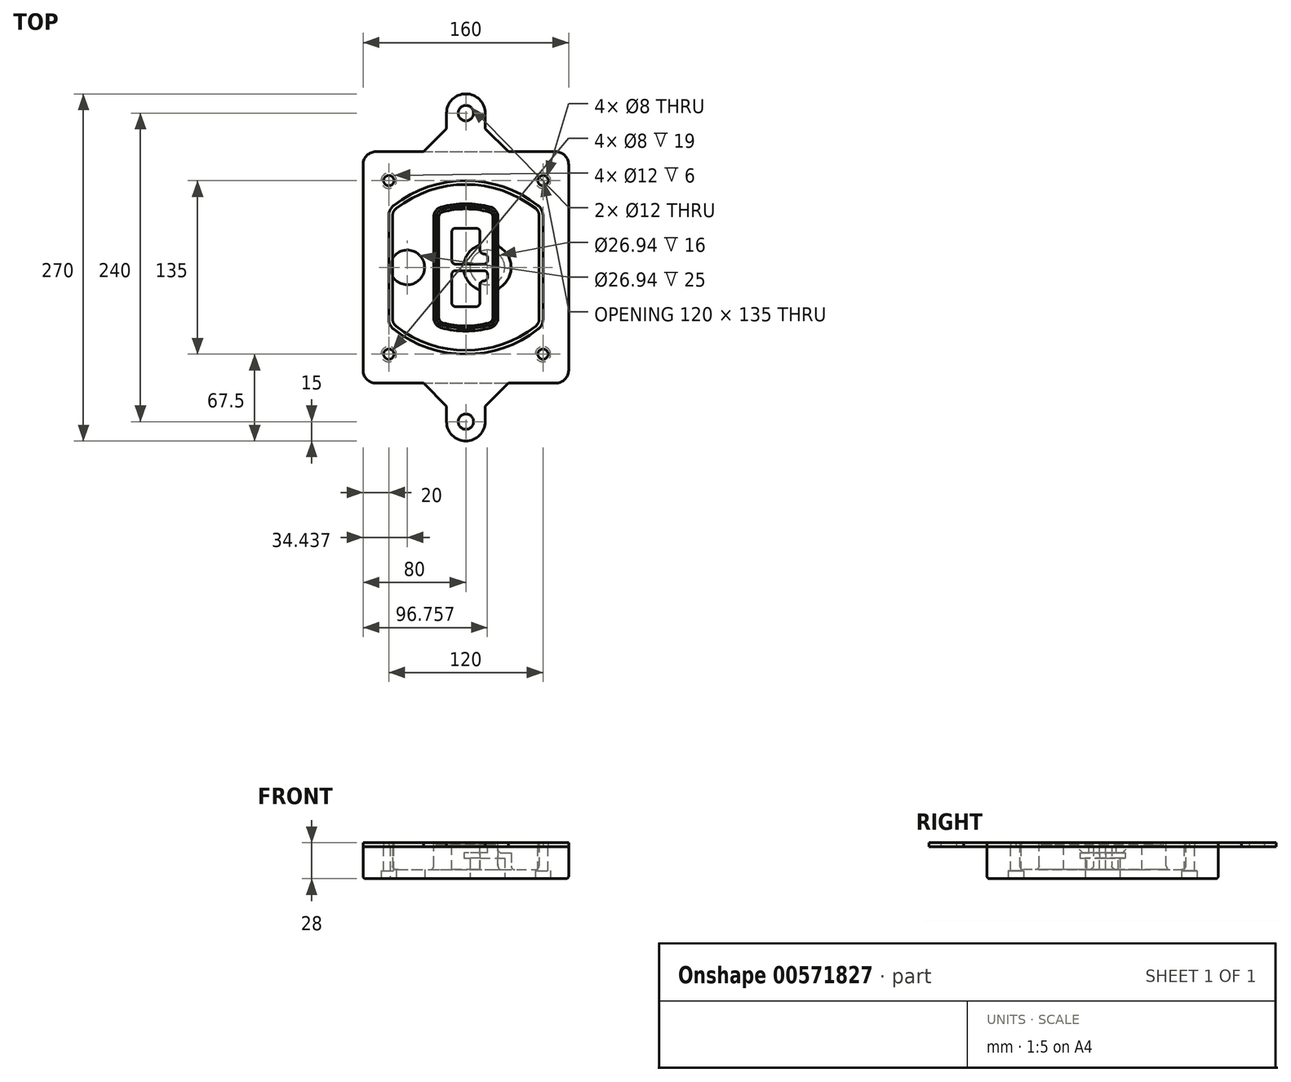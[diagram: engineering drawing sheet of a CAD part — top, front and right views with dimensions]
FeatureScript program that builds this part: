
annotation { "Feature Type Name" : "Feature", "Feature Type Description" : "" }
export const myFeature = defineFeature(function(context is Context, id is Id, definition is map)
    precondition{}
    {
        {
            var Q0;
            Q0=qCreatedBy(makeId("Top.planeOp"),FACE);
            var sketch = newSketch(context, id + "F0", { "sketchPlane" : qUnion([Q0])});
            skPoint(sketch, "E0.rect.middle", {"position": v(0, 0) * mm});
            skLineSegment(sketch, "E1.bottom", {"start": v(-70, -90) * mm, "end": v(70, -90) * mm});
            skLineSegment(sketch, "E1.top", {"start": v(-70, 90) * mm, "end": v(70, 90) * mm});
            skLineSegment(sketch, "E1.left", {"start": v(-80, -80) * mm, "end": v(-80, 80) * mm});
            skLineSegment(sketch, "E1.right", {"start": v(80, -80) * mm, "end": v(80, 80) * mm});
            skLineSegment(sketch, "E2", {"start": v(-80, 90) * mm, "end": v(80, -90) * mm, "construction": true});
            skLineSegment(sketch, "E3", {"start": v(80, 90) * mm, "end": v(-80, -90) * mm, "construction": true});
            skCircle(sketch, "E4", {"center": v(-60, 67.5) * mm, "radius": 4 * mm});
            skCircle(sketch, "E5", {"center": v(60, 67.5) * mm, "radius": 4 * mm});
            skCircle(sketch, "E6", {"center": v(60, -67.5) * mm, "radius": 4 * mm});
            skCircle(sketch, "E7", {"center": v(-60, -67.5) * mm, "radius": 4 * mm});
            skLineSegment(sketch, "E8", {"start": v(-60, 67.5) * mm, "end": v(60, 67.5) * mm, "construction": true});
            skLineSegment(sketch, "E9", {"start": v(60, 67.5) * mm, "end": v(60, -67.5) * mm, "construction": true});
            skLineSegment(sketch, "E10", {"start": v(60, -67.5) * mm, "end": v(-60, -67.5) * mm, "construction": true});
            skLineSegment(sketch, "E11", {"start": v(-60, -67.5) * mm, "end": v(-60, 67.5) * mm, "construction": true});
            skLineSegment(sketch, "E12", {"start": v(-60, 40.3) * mm, "end": v(-60, -40.3) * mm});
            skLineSegment(sketch, "E13", {"start": v(60, 40.3) * mm, "end": v(60, -40.3) * mm});
            skArc(sketch, "E14", {"start": v(56.15, 48.18) * mm, "mid": v(0, 67.5) * mm, "end": v(-56.15, 48.18) * mm});
            skArc(sketch, "E15", {"start": v(-56.15, -48.18) * mm, "mid": v(0, -67.5) * mm, "end": v(56.15, -48.18) * mm});
            skLineSegment(sketch, "E16", {"start": v(-60, 0) * mm, "end": v(60, 0) * mm, "construction": true});
            skPoint(sketch, "E17.visualSharp", {"position": v(-60, -45) * mm});
            skArc(sketch, "E17.filletArc", {"start": v(-60, -40.3) * mm, "mid": v(-58.99, -44.68) * mm, "end": v(-56.15, -48.18) * mm});
            skPoint(sketch, "E18.visualSharp", {"position": v(-60, 45) * mm});
            skArc(sketch, "E18.filletArc", {"start": v(-56.15, 48.18) * mm, "mid": v(-58.99, 44.68) * mm, "end": v(-60, 40.3) * mm});
            skPoint(sketch, "E19.visualSharp", {"position": v(60, 45) * mm});
            skArc(sketch, "E19.filletArc", {"start": v(60, 40.3) * mm, "mid": v(58.99, 44.68) * mm, "end": v(56.15, 48.18) * mm});
            skPoint(sketch, "E20.visualSharp", {"position": v(60, -45) * mm});
            skArc(sketch, "E20.filletArc", {"start": v(56.15, -48.18) * mm, "mid": v(58.99, -44.68) * mm, "end": v(60, -40.3) * mm});
            skPoint(sketch, "E21.visualSharp", {"position": v(-80, 90) * mm});
            skArc(sketch, "E21.filletArc", {"start": v(-70, 90) * mm, "mid": v(-77.07, 87.07) * mm, "end": v(-80, 80) * mm});
            skPoint(sketch, "E22.visualSharp", {"position": v(80, 90) * mm});
            skArc(sketch, "E22.filletArc", {"start": v(80, 80) * mm, "mid": v(77.07, 87.07) * mm, "end": v(70, 90) * mm});
            skPoint(sketch, "E23.visualSharp", {"position": v(80, -90) * mm});
            skArc(sketch, "E23.filletArc", {"start": v(70, -90) * mm, "mid": v(77.07, -87.07) * mm, "end": v(80, -80) * mm});
            skPoint(sketch, "E24.visualSharp", {"position": v(-80, -90) * mm});
            skArc(sketch, "E24.filletArc", {"start": v(-80, -80) * mm, "mid": v(-77.07, -87.07) * mm, "end": v(-70, -90) * mm});
            skArc(sketch, "E25.0", {"start": v(57, 40.3) * mm, "mid": v(56.3, 43.36) * mm, "end": v(54.3, 45.81) * mm});
            skLineSegment(sketch, "E25.1", {"start": v(57, 40.3) * mm, "end": v(57, -40.3) * mm});
            skArc(sketch, "E25.2", {"start": v(54.3, -45.81) * mm, "mid": v(56.3, -43.36) * mm, "end": v(57, -40.3) * mm});
            skArc(sketch, "E25.3", {"start": v(-54.3, -45.81) * mm, "mid": v(0, -64.5) * mm, "end": v(54.3, -45.81) * mm});
            skArc(sketch, "E25.4", {"start": v(-57, -40.3) * mm, "mid": v(-56.3, -43.36) * mm, "end": v(-54.3, -45.81) * mm});
            skArc(sketch, "E25.5", {"start": v(54.3, 45.81) * mm, "mid": v(0, 64.5) * mm, "end": v(-54.3, 45.81) * mm});
            skLineSegment(sketch, "E25.6", {"start": v(-57, 40.3) * mm, "end": v(-57, -40.3) * mm});
            skArc(sketch, "E25.7", {"start": v(-54.3, 45.81) * mm, "mid": v(-56.3, 43.36) * mm, "end": v(-57, 40.3) * mm});
            skArc(sketch, "E26.0", {"start": v(-58.62, 51.33) * mm, "mid": v(-62.58, 46.43) * mm, "end": v(-64, 40.3) * mm});
            skArc(sketch, "E26.1", {"start": v(58.62, 51.33) * mm, "mid": v(0, 71.5) * mm, "end": v(-58.62, 51.33) * mm});
            skArc(sketch, "E26.2", {"start": v(64, 40.3) * mm, "mid": v(62.58, 46.43) * mm, "end": v(58.62, 51.33) * mm});
            skLineSegment(sketch, "E26.3", {"start": v(64, 40.3) * mm, "end": v(64, -40.3) * mm});
            skArc(sketch, "E26.4", {"start": v(58.62, -51.33) * mm, "mid": v(62.58, -46.43) * mm, "end": v(64, -40.3) * mm});
            skLineSegment(sketch, "E26.5", {"start": v(-64, 40.3) * mm, "end": v(-64, -40.3) * mm});
            skArc(sketch, "E26.6", {"start": v(-58.62, -51.33) * mm, "mid": v(0, -71.5) * mm, "end": v(58.62, -51.33) * mm});
            skArc(sketch, "E26.7", {"start": v(-64, -40.3) * mm, "mid": v(-62.58, -46.43) * mm, "end": v(-58.62, -51.33) * mm});
            skSolve(sketch);
        }
        {
            var Q0;
            Q0=makeQuery(id+"F0.imprint","IMPRINT",FACE,{"disambiguationData":[TD([[makeQuery(id+"F0.imprint","IMPRINT",EDGE,{"derivedFrom":sQuery(id+"F0.wireOp",EDGE,"E1.bottom")}),1.0]])]});
            var Q1;
            Q1=makeQuery(id+"F0.imprint","IMPRINT",FACE,{"disambiguationData":[TD([[makeQuery(id+"F0.imprint","IMPRINT",EDGE,{"derivedFrom":sQuery(id+"F0.wireOp",EDGE,"E12")}),1.0]])]});
            var Q2;
            Q2=makeQuery(id+"F0.imprint","IMPRINT",FACE,{"disambiguationData":[TD([[makeQuery(id+"F0.imprint","IMPRINT",EDGE,{"derivedFrom":sQuery(id+"F0.wireOp",EDGE,"E25.0")}),1.0]])]});
            var Q3;
            Q3=makeQuery(id+"F0.imprint","IMPRINT",FACE,{"disambiguationData":[TD([[makeQuery(id+"F0.imprint","IMPRINT",EDGE,{"derivedFrom":sQuery(id+"F0.wireOp",EDGE,"E12")}),-1.0]])]});
            extrude(context, id + "F1", {"entities" : qUnion([Q0, Q1, Q2, Q3]), "oppositeDirection" : true, "depth" : 25 * mm});
        }
        {
            var Q0;
            Q0=makeQuery(id+"F0.imprint","IMPRINT",FACE,{"disambiguationData":[TD([[makeQuery(id+"F0.imprint","IMPRINT",EDGE,{"derivedFrom":sQuery(id+"F0.wireOp",EDGE,"E12")}),1.0]])]});
            extrude(context, id + "F2", {"entities" : qUnion([Q0]), "operationType" : NewBodyOperationType.ADD, "depth" : 3 * mm});
        }
        {
            var Q0;
            Q0=makeQuery(id+"F0.imprint","IMPRINT",FACE,{"disambiguationData":[TD([[makeQuery(id+"F0.imprint","IMPRINT",EDGE,{"derivedFrom":sQuery(id+"F0.wireOp",EDGE,"E25.0")}),1.0]])]});
            extrude(context, id + "F3", {"entities" : qUnion([Q0]), "operationType" : NewBodyOperationType.REMOVE, "oppositeDirection" : true, "depth" : 18 * mm});
        }
        {
            var Q0;
            Q0=makeQuery(id+"F2.opExtrude","CAP_FACE",FACE,{"disambiguationData":[OSD([sQuery(id+"F0.wireOp",EDGE,"E12"),sQuery(id+"F0.wireOp",EDGE,"E13"),sQuery(id+"F0.wireOp",EDGE,"E14"),sQuery(id+"F0.wireOp",EDGE,"E15"),sQuery(id+"F0.wireOp",EDGE,"E17.filletArc"),sQuery(id+"F0.wireOp",EDGE,"E18.filletArc"),sQuery(id+"F0.wireOp",EDGE,"E19.filletArc"),sQuery(id+"F0.wireOp",EDGE,"E20.filletArc"),sQuery(id+"F0.wireOp",EDGE,"E25.0"),sQuery(id+"F0.wireOp",EDGE,"E25.1"),sQuery(id+"F0.wireOp",EDGE,"E25.2"),sQuery(id+"F0.wireOp",EDGE,"E25.3"),sQuery(id+"F0.wireOp",EDGE,"E25.4"),sQuery(id+"F0.wireOp",EDGE,"E25.5"),sQuery(id+"F0.wireOp",EDGE,"E25.6"),sQuery(id+"F0.wireOp",EDGE,"E25.7")])],"isStart":false});
            var sketch = newSketch(context, id + "F4", { "sketchPlane" : qUnion([Q0])});
            skArc(sketch, "E27.0", {"start": v(-19.08, -46.97) * mm, "mid": v(0, -49.5) * mm, "end": v(19.08, -46.97) * mm});
            skArc(sketch, "E28.0", {"start": v(19.08, 46.97) * mm, "mid": v(0, 49.5) * mm, "end": v(-19.08, 46.97) * mm});
            skLineSegment(sketch, "E29", {"start": v(-25, 39.25) * mm, "end": v(-25, -39.25) * mm});
            skLineSegment(sketch, "E30", {"start": v(25, 39.25) * mm, "end": v(25, -39.25) * mm});
            skLineSegment(sketch, "E31", {"start": v(-25, 45.1) * mm, "end": v(25, 45.1) * mm, "construction": true});
            skLineSegment(sketch, "E32", {"start": v(-25, -45.1) * mm, "end": v(25, -45.1) * mm, "construction": true});
            skPoint(sketch, "E33.visualSharp", {"position": v(-25, 45.1) * mm});
            skArc(sketch, "E33.filletArc", {"start": v(-19.08, 46.97) * mm, "mid": v(-23.35, 44.11) * mm, "end": v(-25, 39.25) * mm});
            skPoint(sketch, "E34.visualSharp", {"position": v(25, 45.1) * mm});
            skArc(sketch, "E34.filletArc", {"start": v(25, 39.25) * mm, "mid": v(23.35, 44.11) * mm, "end": v(19.08, 46.97) * mm});
            skPoint(sketch, "E35.visualSharp", {"position": v(25, -45.1) * mm});
            skArc(sketch, "E35.filletArc", {"start": v(19.08, -46.97) * mm, "mid": v(23.35, -44.11) * mm, "end": v(25, -39.25) * mm});
            skPoint(sketch, "E36.visualSharp", {"position": v(-25, -45.1) * mm});
            skArc(sketch, "E36.filletArc", {"start": v(-25, -39.25) * mm, "mid": v(-23.35, -44.11) * mm, "end": v(-19.08, -46.97) * mm});
            skArc(sketch, "E37.0", {"start": v(54.3, 45.81) * mm, "mid": v(0, 64.5) * mm, "end": v(-54.3, 45.81) * mm});
            skArc(sketch, "E37.1", {"start": v(-54.3, 45.81) * mm, "mid": v(-56.3, 43.36) * mm, "end": v(-57, 40.3) * mm});
            skLineSegment(sketch, "E37.2", {"start": v(-57, 40.3) * mm, "end": v(-57, -40.3) * mm});
            skArc(sketch, "E37.3", {"start": v(-57, -40.3) * mm, "mid": v(-56.3, -43.36) * mm, "end": v(-54.3, -45.81) * mm});
            skArc(sketch, "E37.4", {"start": v(-54.3, -45.81) * mm, "mid": v(0, -64.5) * mm, "end": v(54.3, -45.81) * mm});
            skArc(sketch, "E37.5", {"start": v(54.3, -45.81) * mm, "mid": v(56.3, -43.36) * mm, "end": v(57, -40.3) * mm});
            skLineSegment(sketch, "E37.6", {"start": v(57, 40.3) * mm, "end": v(57, -40.3) * mm});
            skArc(sketch, "E37.7", {"start": v(57, 40.3) * mm, "mid": v(56.3, 43.36) * mm, "end": v(54.3, 45.81) * mm});
            skLineSegment(sketch, "E38.0", {"start": v(23, 39.25) * mm, "end": v(23, -39.25) * mm});
            skArc(sketch, "E38.1", {"start": v(18.56, -45.04) * mm, "mid": v(21.76, -42.9) * mm, "end": v(23, -39.25) * mm});
            skArc(sketch, "E38.2", {"start": v(-18.56, -45.04) * mm, "mid": v(0, -47.5) * mm, "end": v(18.56, -45.04) * mm});
            skArc(sketch, "E38.3", {"start": v(-23, -39.25) * mm, "mid": v(-21.76, -42.9) * mm, "end": v(-18.56, -45.04) * mm});
            skLineSegment(sketch, "E38.4", {"start": v(-23, 39.25) * mm, "end": v(-23, -39.25) * mm});
            skArc(sketch, "E38.5", {"start": v(23, 39.25) * mm, "mid": v(21.76, 42.9) * mm, "end": v(18.56, 45.04) * mm});
            skArc(sketch, "E38.6", {"start": v(-18.56, 45.04) * mm, "mid": v(-21.76, 42.9) * mm, "end": v(-23, 39.25) * mm});
            skArc(sketch, "E38.7", {"start": v(18.56, 45.04) * mm, "mid": v(0, 47.5) * mm, "end": v(-18.56, 45.04) * mm});
            skArc(sketch, "E39.0", {"start": v(21, 39.25) * mm, "mid": v(20.18, 41.68) * mm, "end": v(18.04, 43.1) * mm});
            skLineSegment(sketch, "E39.1", {"start": v(21, 39.25) * mm, "end": v(21, -39.25) * mm});
            skArc(sketch, "E39.2", {"start": v(18.04, -43.1) * mm, "mid": v(20.18, -41.68) * mm, "end": v(21, -39.25) * mm});
            skArc(sketch, "E39.3", {"start": v(-18.04, -43.1) * mm, "mid": v(0, -45.5) * mm, "end": v(18.04, -43.1) * mm});
            skArc(sketch, "E39.4", {"start": v(-21, -39.25) * mm, "mid": v(-20.18, -41.68) * mm, "end": v(-18.04, -43.1) * mm});
            skArc(sketch, "E39.5", {"start": v(18.04, 43.1) * mm, "mid": v(0, 45.5) * mm, "end": v(-18.04, 43.1) * mm});
            skLineSegment(sketch, "E39.6", {"start": v(-21, 39.25) * mm, "end": v(-21, -39.25) * mm});
            skArc(sketch, "E39.7", {"start": v(-18.04, 43.1) * mm, "mid": v(-20.18, 41.68) * mm, "end": v(-21, 39.25) * mm});
            skLineSegment(sketch, "E40", {"start": v(-25, 0) * mm, "end": v(25, 0) * mm, "construction": true});
            skLineSegment(sketch, "E41", {"start": v(-11, 5.5) * mm, "end": v(-11, 27.5) * mm});
            skLineSegment(sketch, "E42", {"start": v(-8, 30.5) * mm, "end": v(8, 30.5) * mm});
            skLineSegment(sketch, "E43", {"start": v(11, 27.5) * mm, "end": v(11, 13.5) * mm});
            skLineSegment(sketch, "E44", {"start": v(14, 10.5) * mm, "end": v(14, 10.5) * mm});
            skLineSegment(sketch, "E45", {"start": v(17, 7.5) * mm, "end": v(17, 5.5) * mm});
            skLineSegment(sketch, "E46", {"start": v(14, 2.5) * mm, "end": v(-8, 2.5) * mm});
            skPoint(sketch, "E47.visualSharp", {"position": v(-11, 30.5) * mm});
            skArc(sketch, "E47.filletArc", {"start": v(-8, 30.5) * mm, "mid": v(-10.12, 29.62) * mm, "end": v(-11, 27.5) * mm});
            skPoint(sketch, "E48.visualSharp", {"position": v(11, 30.5) * mm});
            skArc(sketch, "E48.filletArc", {"start": v(11, 27.5) * mm, "mid": v(10.12, 29.62) * mm, "end": v(8, 30.5) * mm});
            skPoint(sketch, "E49.visualSharp", {"position": v(11, 10.5) * mm});
            skArc(sketch, "E49.filletArc", {"start": v(11, 13.5) * mm, "mid": v(11.88, 11.38) * mm, "end": v(14, 10.5) * mm});
            skPoint(sketch, "E50.visualSharp", {"position": v(17, 10.5) * mm});
            skArc(sketch, "E50.filletArc", {"start": v(17, 7.5) * mm, "mid": v(16.12, 9.62) * mm, "end": v(14, 10.5) * mm});
            skPoint(sketch, "E51.visualSharp", {"position": v(17, 2.5) * mm});
            skArc(sketch, "E51.filletArc", {"start": v(14, 2.5) * mm, "mid": v(16.12, 3.38) * mm, "end": v(17, 5.5) * mm});
            skPoint(sketch, "E52.visualSharp", {"position": v(-11, 2.5) * mm});
            skArc(sketch, "E52.filletArc", {"start": v(-11, 5.5) * mm, "mid": v(-10.12, 3.38) * mm, "end": v(-8, 2.5) * mm});
            skLineSegment(sketch, "E53.0.MirrorCS", {"start": v(14, -2.5) * mm, "end": v(-8, -2.5) * mm});
            skArc(sketch, "E54.0.MirrorCS", {"start": v(-11, -5.5) * mm, "mid": v(-10.12, -3.38) * mm, "end": v(-8, -2.5) * mm});
            skLineSegment(sketch, "E55.0.MirrorCS", {"start": v(-11, -5.5) * mm, "end": v(-11, -27.5) * mm});
            skArc(sketch, "E56.0.MirrorCS", {"start": v(-8, -30.5) * mm, "mid": v(-10.12, -29.62) * mm, "end": v(-11, -27.5) * mm});
            skLineSegment(sketch, "E57.0.MirrorCS", {"start": v(-8, -30.5) * mm, "end": v(8, -30.5) * mm});
            skArc(sketch, "E58.0.MirrorCS", {"start": v(11, -27.5) * mm, "mid": v(10.12, -29.62) * mm, "end": v(8, -30.5) * mm});
            skLineSegment(sketch, "E59.0.MirrorCS", {"start": v(11, -27.5) * mm, "end": v(11, -13.5) * mm});
            skArc(sketch, "E60.0.MirrorCS", {"start": v(11, -13.5) * mm, "mid": v(11.88, -11.38) * mm, "end": v(14, -10.5) * mm});
            skArc(sketch, "E61.0.MirrorCS", {"start": v(17, -7.5) * mm, "mid": v(16.12, -9.62) * mm, "end": v(14, -10.5) * mm});
            skLineSegment(sketch, "E62.0.MirrorCS", {"start": v(17, -7.5) * mm, "end": v(17, -5.5) * mm});
            skArc(sketch, "E63.0.MirrorCS", {"start": v(14, -2.5) * mm, "mid": v(16.12, -3.38) * mm, "end": v(17, -5.5) * mm});
            skSolve(sketch);
        }
        {
            var Q0;
            Q0=makeQuery(id+"F4.imprint","IMPRINT",FACE,{"disambiguationData":[TD([[makeQuery(id+"F4.imprint","IMPRINT",EDGE,{"derivedFrom":sQuery(id+"F4.wireOp",EDGE,"E27.0")}),1.0]])]});
            var Q1;
            Q1=makeQuery(id+"F4.imprint","IMPRINT",FACE,{"disambiguationData":[TD([[makeQuery(id+"F4.imprint","IMPRINT",EDGE,{"derivedFrom":sQuery(id+"F4.wireOp",EDGE,"E38.0")}),-1.0]])]});
            var Q2;
            Q2=makeQuery(id+"F4.imprint","IMPRINT",FACE,{"disambiguationData":[TD([[makeQuery(id+"F4.imprint","IMPRINT",EDGE,{"derivedFrom":sQuery(id+"F4.wireOp",EDGE,"E39.0")}),1.0]])]});
            extrude(context, id + "F5", {"entities" : qUnion([Q0, Q1, Q2]), "operationType" : NewBodyOperationType.ADD, "endBound" : BoundingType.UP_TO_NEXT, "oppositeDirection" : true, "depth" : 25 * mm});
        }
        {
            var Q0;
            Q0=makeQuery(id+"F4.imprint","IMPRINT",FACE,{"disambiguationData":[TD([[makeQuery(id+"F4.imprint","IMPRINT",EDGE,{"derivedFrom":sQuery(id+"F4.wireOp",EDGE,"E38.0")}),-1.0]])]});
            extrude(context, id + "F6", {"entities" : qUnion([Q0]), "operationType" : NewBodyOperationType.REMOVE, "oppositeDirection" : true, "depth" : 2 * mm});
        }
        {
            var Q0;
            Q0=makeQuery(id+"F1.opExtrude","CAP_FACE",FACE,{"disambiguationData":[OSD([sQuery(id+"F0.wireOp",EDGE,"E1.bottom"),sQuery(id+"F0.wireOp",EDGE,"E1.top"),sQuery(id+"F0.wireOp",EDGE,"E1.left"),sQuery(id+"F0.wireOp",EDGE,"E1.right"),sQuery(id+"F0.wireOp",EDGE,"E4"),sQuery(id+"F0.wireOp",EDGE,"E5"),sQuery(id+"F0.wireOp",EDGE,"E6"),sQuery(id+"F0.wireOp",EDGE,"E7"),sQuery(id+"F0.wireOp",EDGE,"E21.filletArc"),sQuery(id+"F0.wireOp",EDGE,"E22.filletArc"),sQuery(id+"F0.wireOp",EDGE,"E23.filletArc"),sQuery(id+"F0.wireOp",EDGE,"E24.filletArc")])],"isStart":false});
            var sketch = newSketch(context, id + "F7", { "sketchPlane" : qUnion([Q0])});
            skCircle(sketch, "E64", {"center": v(16.76, 0) * mm, "radius": 13.47 * mm});
            skCircle(sketch, "E65", {"center": v(-45.56, 0) * mm, "radius": 13.47 * mm});
            skLineSegment(sketch, "E66", {"start": v(80, 0) * mm, "end": v(-80, 0) * mm});
            skCircle(sketch, "E67", {"center": v(16.76, 0) * mm, "radius": 18.47 * mm});
            skCircle(sketch, "E68", {"center": v(60, -67.5) * mm, "radius": 6 * mm});
            skCircle(sketch, "E69", {"center": v(-60, -67.5) * mm, "radius": 6 * mm});
            skCircle(sketch, "E70", {"center": v(-60, 67.5) * mm, "radius": 6 * mm});
            skCircle(sketch, "E71", {"center": v(60, 67.5) * mm, "radius": 6 * mm});
            skSolve(sketch);
        }
        {
            var Q0;
            {var subQ1=sQuery(id+"F7.wireOp",EDGE,"E66");var subQ4=sQuery(id+"F7.wireOp",EDGE,"E64");var subQ6=makeQuery(id+"F7.imprint","INTERSECT",VERTEX,{"disambiguationData":[OD(0.0)],"derivedFrom":[subQ4,subQ1]});Q0=makeQuery(id+"F7.imprint","IMPRINT",FACE,{"disambiguationData":[TD([[makeQuery(id+"F7.imprint","IMPRINT",EDGE,{"disambiguationData":[TD([[subQ6,-1.0]])],"derivedFrom":subQ4}),-1.0]])]});}
            var Q1;
            {var subQ0=sQuery(id+"F7.wireOp",EDGE,"E66");var subQ1=sQuery(id+"F7.wireOp",EDGE,"E64");var subQ3=makeQuery(id+"F7.imprint","INTERSECT",VERTEX,{"disambiguationData":[OD(0.0)],"derivedFrom":[subQ1,subQ0]});Q1=makeQuery(id+"F7.imprint","IMPRINT",FACE,{"disambiguationData":[TD([[makeQuery(id+"F7.imprint","IMPRINT",EDGE,{"disambiguationData":[TD([[subQ3,-1.0]])],"derivedFrom":subQ1}),1.0]])]});}
            var Q2;
            {var subQ0=sQuery(id+"F7.wireOp",EDGE,"E66");var subQ1=sQuery(id+"F7.wireOp",EDGE,"E64");var subQ3=makeQuery(id+"F7.imprint","INTERSECT",VERTEX,{"disambiguationData":[OD(0.0)],"derivedFrom":[subQ1,subQ0]});Q2=makeQuery(id+"F7.imprint","IMPRINT",FACE,{"disambiguationData":[TD([[makeQuery(id+"F7.imprint","IMPRINT",EDGE,{"disambiguationData":[TD([[subQ3,1.0]])],"derivedFrom":subQ1}),1.0]])]});}
            var Q3;
            {var subQ1=sQuery(id+"F7.wireOp",EDGE,"E66");var subQ4=sQuery(id+"F7.wireOp",EDGE,"E64");var subQ6=makeQuery(id+"F7.imprint","INTERSECT",VERTEX,{"disambiguationData":[OD(0.0)],"derivedFrom":[subQ4,subQ1]});Q3=makeQuery(id+"F7.imprint","IMPRINT",FACE,{"disambiguationData":[TD([[makeQuery(id+"F7.imprint","IMPRINT",EDGE,{"disambiguationData":[TD([[subQ6,1.0]])],"derivedFrom":subQ4}),-1.0]])]});}
            extrude(context, id + "F8", {"entities" : qUnion([Q0, Q1, Q2, Q3]), "operationType" : NewBodyOperationType.ADD, "oppositeDirection" : true, "depth" : 20 * mm});
        }
        {
            var Q0;
            {var subQ0=sQuery(id+"F7.wireOp",EDGE,"E66");var subQ1=sQuery(id+"F7.wireOp",EDGE,"E64");var subQ3=makeQuery(id+"F7.imprint","INTERSECT",VERTEX,{"disambiguationData":[OD(0.0)],"derivedFrom":[subQ1,subQ0]});Q0=makeQuery(id+"F7.imprint","IMPRINT",FACE,{"disambiguationData":[TD([[makeQuery(id+"F7.imprint","IMPRINT",EDGE,{"disambiguationData":[TD([[subQ3,-1.0]])],"derivedFrom":subQ1}),1.0]])]});}
            var Q1;
            {var subQ0=sQuery(id+"F7.wireOp",EDGE,"E66");var subQ1=sQuery(id+"F7.wireOp",EDGE,"E64");var subQ3=makeQuery(id+"F7.imprint","INTERSECT",VERTEX,{"disambiguationData":[OD(0.0)],"derivedFrom":[subQ1,subQ0]});Q1=makeQuery(id+"F7.imprint","IMPRINT",FACE,{"disambiguationData":[TD([[makeQuery(id+"F7.imprint","IMPRINT",EDGE,{"disambiguationData":[TD([[subQ3,1.0]])],"derivedFrom":subQ1}),1.0]])]});}
            extrude(context, id + "F9", {"entities" : qUnion([Q0, Q1]), "operationType" : NewBodyOperationType.REMOVE, "oppositeDirection" : true, "depth" : 16 * mm});
        }
        {
            var Q0;
            {var subQ0=sQuery(id+"F7.wireOp",EDGE,"E66");var subQ1=sQuery(id+"F7.wireOp",EDGE,"E65");var subQ3=makeQuery(id+"F7.imprint","INTERSECT",VERTEX,{"disambiguationData":[OD(0.0)],"derivedFrom":[subQ1,subQ0]});Q0=makeQuery(id+"F7.imprint","IMPRINT",FACE,{"disambiguationData":[TD([[makeQuery(id+"F7.imprint","IMPRINT",EDGE,{"disambiguationData":[TD([[subQ3,-1.0]])],"derivedFrom":subQ1}),1.0]])]});}
            var Q1;
            {var subQ0=sQuery(id+"F7.wireOp",EDGE,"E66");var subQ1=sQuery(id+"F7.wireOp",EDGE,"E65");var subQ3=makeQuery(id+"F7.imprint","INTERSECT",VERTEX,{"disambiguationData":[OD(0.0)],"derivedFrom":[subQ1,subQ0]});Q1=makeQuery(id+"F7.imprint","IMPRINT",FACE,{"disambiguationData":[TD([[makeQuery(id+"F7.imprint","IMPRINT",EDGE,{"disambiguationData":[TD([[subQ3,1.0]])],"derivedFrom":subQ1}),1.0]])]});}
            extrude(context, id + "F10", {"entities" : qUnion([Q0, Q1]), "operationType" : NewBodyOperationType.REMOVE, "oppositeDirection" : true, "depth" : 25 * mm});
        }
        {
            var Q0;
            Q0=makeQuery(id+"F7.imprint","IMPRINT",FACE,{"disambiguationData":[TD([[makeQuery(id+"F7.imprint","IMPRINT",EDGE,{"derivedFrom":sQuery(id+"F7.wireOp",EDGE,"E68")}),1.0]])]});
            var Q1;
            Q1=makeQuery(id+"F7.imprint","IMPRINT",FACE,{"disambiguationData":[TD([[makeQuery(id+"F7.imprint","IMPRINT",EDGE,{"derivedFrom":makeQuery(id+"F1.opExtrude","CAP_EDGE",EDGE,{"disambiguationData":[OSD([sQuery(id+"F0.wireOp",EDGE,"E5")])],"isStart":false})}),-1.0]])]});
            var Q2;
            Q2=makeQuery(id+"F7.imprint","IMPRINT",FACE,{"disambiguationData":[TD([[makeQuery(id+"F7.imprint","IMPRINT",EDGE,{"derivedFrom":sQuery(id+"F7.wireOp",EDGE,"E69")}),1.0]])]});
            var Q3;
            Q3=makeQuery(id+"F7.imprint","IMPRINT",FACE,{"disambiguationData":[TD([[makeQuery(id+"F7.imprint","IMPRINT",EDGE,{"derivedFrom":makeQuery(id+"F1.opExtrude","CAP_EDGE",EDGE,{"disambiguationData":[OSD([sQuery(id+"F0.wireOp",EDGE,"E4")])],"isStart":false})}),-1.0]])]});
            var Q4;
            Q4=makeQuery(id+"F7.imprint","IMPRINT",FACE,{"disambiguationData":[TD([[makeQuery(id+"F7.imprint","IMPRINT",EDGE,{"derivedFrom":sQuery(id+"F7.wireOp",EDGE,"E70")}),1.0]])]});
            var Q5;
            Q5=makeQuery(id+"F7.imprint","IMPRINT",FACE,{"disambiguationData":[TD([[makeQuery(id+"F7.imprint","IMPRINT",EDGE,{"derivedFrom":makeQuery(id+"F1.opExtrude","CAP_EDGE",EDGE,{"disambiguationData":[OSD([sQuery(id+"F0.wireOp",EDGE,"E7")])],"isStart":false})}),-1.0]])]});
            var Q6;
            Q6=makeQuery(id+"F7.imprint","IMPRINT",FACE,{"disambiguationData":[TD([[makeQuery(id+"F7.imprint","IMPRINT",EDGE,{"derivedFrom":sQuery(id+"F7.wireOp",EDGE,"E71")}),1.0]])]});
            var Q7;
            Q7=makeQuery(id+"F7.imprint","IMPRINT",FACE,{"disambiguationData":[TD([[makeQuery(id+"F7.imprint","IMPRINT",EDGE,{"derivedFrom":makeQuery(id+"F1.opExtrude","CAP_EDGE",EDGE,{"disambiguationData":[OSD([sQuery(id+"F0.wireOp",EDGE,"E6")])],"isStart":false})}),-1.0]])]});
            extrude(context, id + "F11", {"entities" : qUnion([Q0, Q1, Q2, Q3, Q4, Q5, Q6, Q7]), "operationType" : NewBodyOperationType.REMOVE, "oppositeDirection" : true, "depth" : 6 * mm});
        }
        {
            var Q0;
            Q0=makeQuery(id+"F9.boolean.opBoolean","COPY",FACE,{"derivedFrom":makeQuery(id+"F9.opExtrude","CAP_FACE",FACE,{"disambiguationData":[OSD([sQuery(id+"F7.wireOp",EDGE,"E64")])],"isStart":false})});
            var sketch = newSketch(context, id + "F12", { "sketchPlane" : qUnion([Q0])});
            skArc(sketch, "E72.0", {"start": v(11, 17.55) * mm, "mid": v(2.57, 11.82) * mm, "end": v(-1.54, 2.5) * mm});
            skArc(sketch, "E72.1", {"start": v(-1.54, -2.5) * mm, "mid": v(2.57, -11.82) * mm, "end": v(11, -17.55) * mm});
            skLineSegment(sketch, "E73", {"start": v(-1.54, -2.5) * mm, "end": v(14, -2.5) * mm});
            skLineSegment(sketch, "E74.0", {"start": v(14, 2.5) * mm, "end": v(-1.54, 2.5) * mm});
            skArc(sketch, "E74.1", {"start": v(14, 2.5) * mm, "mid": v(16.12, 3.38) * mm, "end": v(17, 5.5) * mm});
            skLineSegment(sketch, "E74.2", {"start": v(17, 7.5) * mm, "end": v(17, 5.5) * mm});
            skArc(sketch, "E74.3", {"start": v(17, 7.5) * mm, "mid": v(16.12, 9.62) * mm, "end": v(14, 10.5) * mm});
            skArc(sketch, "E74.4", {"start": v(11, 13.5) * mm, "mid": v(11.88, 11.38) * mm, "end": v(14, 10.5) * mm});
            skLineSegment(sketch, "E74.5", {"start": v(11, 17.55) * mm, "end": v(11, 13.5) * mm});
            skLineSegment(sketch, "E74.7", {"start": v(14, -2.5) * mm, "end": v(-1.54, -2.5) * mm});
            skArc(sketch, "E74.8", {"start": v(14, -2.5) * mm, "mid": v(16.12, -3.38) * mm, "end": v(17, -5.5) * mm});
            skLineSegment(sketch, "E74.9", {"start": v(17, -7.5) * mm, "end": v(17, -5.5) * mm});
            skArc(sketch, "E74.10", {"start": v(17, -7.5) * mm, "mid": v(16.12, -9.62) * mm, "end": v(14, -10.5) * mm});
            skArc(sketch, "E74.11", {"start": v(11, -13.5) * mm, "mid": v(11.88, -11.38) * mm, "end": v(14, -10.5) * mm});
            skLineSegment(sketch, "E74.12", {"start": v(11, -17.55) * mm, "end": v(11, -13.5) * mm});
            skPoint(sketch, "E75.orphan", {"position": v(11, -27.5) * mm});
            skPoint(sketch, "E76.orphan", {"position": v(-8, -2.5) * mm});
            skPoint(sketch, "E77.orphan", {"position": v(-8, 2.5) * mm});
            skPoint(sketch, "E78.orphan", {"position": v(11, 27.5) * mm});
            skSolve(sketch);
        }
        {
            var Q0;
            {var subQ7=sQuery(id+"F12.wireOp",EDGE,"E72.0");var subQ14=sQuery(id+"F12.wireOp",EDGE,"E72.1");var subQ16=sQuery(id+"F12.wireOp",EDGE,"E74.1");var subQ18=sQuery(id+"F12.wireOp",EDGE,"E74.8");Q0=qUnion([makeQuery(id+"F12.imprint","IMPRINT",FACE,{"disambiguationData":[TD([[makeQuery(id+"F12.imprint","IMPRINT",EDGE,{"derivedFrom":subQ7}),1.0]])]}),makeQuery(id+"F12.imprint","IMPRINT",FACE,{"disambiguationData":[TD([[makeQuery(id+"F12.imprint","IMPRINT",EDGE,{"derivedFrom":subQ14}),1.0]])]}),makeQuery(id+"F12.imprint","IMPRINT",FACE,{"disambiguationData":[TD([[makeQuery(id+"F12.imprint","IMPRINT",EDGE,{"derivedFrom":subQ16}),1.0]])]}),makeQuery(id+"F12.imprint","IMPRINT",FACE,{"disambiguationData":[TD([[makeQuery(id+"F12.imprint","IMPRINT",EDGE,{"derivedFrom":subQ18}),-1.0]])]})]);}
            var Q1;
            Q1=makeQuery(id+"F5.boolean.opBoolean","SPLIT",FACE,{"disambiguationData":[TD([makeQuery(id+"F5.opExtrude","SWEPT_FACE",FACE,{"disambiguationData":[OSD([sQuery(id+"F4.wireOp",EDGE,"E41")])]})])],"derivedFrom":makeQuery(id+"F3.boolean.opBoolean","COPY",FACE,{"derivedFrom":makeQuery(id+"F3.opExtrude","CAP_FACE",FACE,{"disambiguationData":[OSD([sQuery(id+"F0.wireOp",EDGE,"E25.0"),sQuery(id+"F0.wireOp",EDGE,"E25.1"),sQuery(id+"F0.wireOp",EDGE,"E25.2"),sQuery(id+"F0.wireOp",EDGE,"E25.3"),sQuery(id+"F0.wireOp",EDGE,"E25.4"),sQuery(id+"F0.wireOp",EDGE,"E25.5"),sQuery(id+"F0.wireOp",EDGE,"E25.6"),sQuery(id+"F0.wireOp",EDGE,"E25.7")])],"isStart":false})})});
            extrude(context, id + "F13", {"entities" : qUnion([Q0]), "operationType" : NewBodyOperationType.REMOVE, "endBound" : BoundingType.UP_TO_SURFACE, "endBoundEntityFace" : qUnion([Q1]), "depth" : 25 * mm});
        }
        {
            var Q0;
            Q0=makeQuery(id+"F3.boolean.opBoolean","COPY",EDGE,{"derivedFrom":makeQuery(id+"F3.opExtrude","CAP_EDGE",EDGE,{"disambiguationData":[OSD([sQuery(id+"F0.wireOp",EDGE,"E25.6")])],"isStart":false})});
            var Q1;
            Q1=makeQuery(id+"F8.boolean.opBoolean","INTERSECT",EDGE,{"derivedFrom":[makeQuery(id+"F5.opExtrude","SWEPT_FACE",FACE,{"disambiguationData":[OSD([sQuery(id+"F4.wireOp",EDGE,"E30")])]}),makeQuery(id+"F8.opExtrude","CAP_FACE",FACE,{"disambiguationData":[OSD([sQuery(id+"F7.wireOp",EDGE,"E67")])],"isStart":false})]});
            var Q2;
            Q2=makeQuery(id+"F8.boolean.opBoolean","INTERSECT",EDGE,{"disambiguationData":[OD(1.0)],"derivedFrom":[makeQuery(id+"F5.opExtrude","SWEPT_FACE",FACE,{"disambiguationData":[OSD([sQuery(id+"F4.wireOp",EDGE,"E30")])]}),makeQuery(id+"F8.opExtrude","SWEPT_FACE",FACE,{"disambiguationData":[OSD([sQuery(id+"F7.wireOp",EDGE,"E67")])]})]});
            var Q3;
            {var subQ0=sQuery(id+"F4.wireOp",EDGE,"E30");Q3=makeQuery(id+"F8.boolean.opBoolean","SPLIT",EDGE,{"disambiguationData":[TD([makeQuery(id+"F5.opExtrude","SWEPT_FACE",FACE,{"disambiguationData":[OSD([sQuery(id+"F4.wireOp",EDGE,"E35.filletArc")])]})])],"derivedFrom":makeQuery(id+"F5.opExtrude","CAP_EDGE",EDGE,{"disambiguationData":[OSD([subQ0])],"isStart":false})});}
            var Q4;
            {var subQ0=sQuery(id+"F0.wireOp",EDGE,"E25.7");var subQ1=sQuery(id+"F0.wireOp",EDGE,"E25.1");var subQ2=sQuery(id+"F0.wireOp",EDGE,"E25.6");var subQ3=sQuery(id+"F0.wireOp",EDGE,"E25.5");var subQ4=sQuery(id+"F0.wireOp",EDGE,"E25.4");var subQ5=sQuery(id+"F0.wireOp",EDGE,"E25.0");var subQ6=sQuery(id+"F0.wireOp",EDGE,"E25.2");var subQ7=sQuery(id+"F0.wireOp",EDGE,"E25.3");Q4=makeQuery(id+"F8.boolean.opBoolean","INTERSECT",EDGE,{"derivedFrom":[makeQuery(id+"F5.boolean.opBoolean","SPLIT",FACE,{"disambiguationData":[TD([makeQuery(id+"F2.opExtrude","SWEPT_FACE",FACE,{"disambiguationData":[OSD([subQ5])]})])],"derivedFrom":makeQuery(id+"F3.boolean.opBoolean","COPY",FACE,{"derivedFrom":makeQuery(id+"F3.opExtrude","CAP_FACE",FACE,{"disambiguationData":[OSD([subQ5,subQ1,subQ6,subQ7,subQ4,subQ3,subQ2,subQ0])],"isStart":false})})}),makeQuery(id+"F8.opExtrude","SWEPT_FACE",FACE,{"disambiguationData":[OSD([sQuery(id+"F7.wireOp",EDGE,"E67")])]})]});}
            var Q5;
            Q5=makeQuery(id+"F8.boolean.opBoolean","INTERSECT",EDGE,{"disambiguationData":[OD(0.0)],"derivedFrom":[makeQuery(id+"F5.opExtrude","SWEPT_FACE",FACE,{"disambiguationData":[OSD([sQuery(id+"F4.wireOp",EDGE,"E30")])]}),makeQuery(id+"F8.opExtrude","SWEPT_FACE",FACE,{"disambiguationData":[OSD([sQuery(id+"F7.wireOp",EDGE,"E67")])]})]});
            fillet(context, id + "F14", {"entities" : qUnion([Q0, Q1, Q2, Q3, Q4, Q5]), "radius" : 3 * mm, "tangentPropagation" : true, "allowEdgeOverflow" : false});
        }
        {
            var Q0;
            Q0=makeQuery(id+"F1.opExtrude","CAP_EDGE",EDGE,{"disambiguationData":[OSD([sQuery(id+"F0.wireOp",EDGE,"E1.bottom")])],"isStart":false});
            fillet(context, id + "F15", {"entities" : qUnion([Q0]), "radius" : 2 * mm, "tangentPropagation" : true, "allowEdgeOverflow" : false});
        }
        {
            var Q0;
            {var subQ0=sQuery(id+"F0.wireOp",EDGE,"E21.filletArc");var subQ1=sQuery(id+"F0.wireOp",EDGE,"E7");var subQ2=sQuery(id+"F0.wireOp",EDGE,"E6");var subQ3=sQuery(id+"F0.wireOp",EDGE,"E5");var subQ4=sQuery(id+"F0.wireOp",EDGE,"E4");var subQ5=sQuery(id+"F0.wireOp",EDGE,"E22.filletArc");var subQ6=sQuery(id+"F0.wireOp",EDGE,"E1.bottom");var subQ7=sQuery(id+"F0.wireOp",EDGE,"E1.right");var subQ8=sQuery(id+"F0.wireOp",EDGE,"E1.top");var subQ9=sQuery(id+"F0.wireOp",EDGE,"E1.left");var subQ10=sQuery(id+"F0.wireOp",EDGE,"E23.filletArc");var subQ11=sQuery(id+"F0.wireOp",EDGE,"E24.filletArc");Q0=makeQuery(id+"F2.boolean.opBoolean","SPLIT",FACE,{"disambiguationData":[TD([makeQuery(id+"F1.opExtrude","SWEPT_FACE",FACE,{"disambiguationData":[OSD([subQ6])]})])],"derivedFrom":makeQuery(id+"F1.opExtrude","CAP_FACE",FACE,{"disambiguationData":[OSD([subQ6,subQ8,subQ9,subQ7,subQ4,subQ3,subQ2,subQ1,subQ0,subQ5,subQ10,subQ11])],"isStart":true})});}
            var sketch = newSketch(context, id + "F16", { "sketchPlane" : qUnion([Q0])});
            skLineSegment(sketch, "E79", {"start": v(0, 90) * mm, "end": v(0, 120) * mm, "construction": true});
            skCircle(sketch, "E80", {"center": v(0, 120) * mm, "radius": 6 * mm});
            skArc(sketch, "E81", {"start": v(15, 120) * mm, "mid": v(0, 135) * mm, "end": v(-15, 120) * mm});
            skLineSegment(sketch, "E82", {"start": v(-15, 120) * mm, "end": v(-15, 108) * mm});
            skLineSegment(sketch, "E83", {"start": v(15, 120) * mm, "end": v(15, 108) * mm});
            skLineSegment(sketch, "E84", {"start": v(-15, 108) * mm, "end": v(-33, 90) * mm});
            skLineSegment(sketch, "E85", {"start": v(15, 108) * mm, "end": v(33, 90) * mm});
            skLineSegment(sketch, "E86", {"start": v(-33, 90) * mm, "end": v(33, 90) * mm});
            skLineSegment(sketch, "E87", {"start": v(-80, 0) * mm, "end": v(80, 0) * mm, "construction": true});
            skLineSegment(sketch, "E88.MirrorCS", {"start": v(-33, -90) * mm, "end": v(33, -90) * mm});
            skLineSegment(sketch, "E89.MirrorCS", {"start": v(-15, -108) * mm, "end": v(-33, -90) * mm});
            skLineSegment(sketch, "E90.MirrorCS", {"start": v(-15, -120) * mm, "end": v(-15, -108) * mm});
            skArc(sketch, "E91.MirrorCS", {"start": v(15, -120) * mm, "mid": v(0, -135) * mm, "end": v(-15, -120) * mm});
            skLineSegment(sketch, "E92.MirrorCS", {"start": v(15, -120) * mm, "end": v(15, -108) * mm});
            skLineSegment(sketch, "E93.MirrorCS", {"start": v(15, -108) * mm, "end": v(33, -90) * mm});
            skLineSegment(sketch, "E94.MirrorCS", {"start": v(0, -90) * mm, "end": v(0, -120) * mm, "construction": true});
            skCircle(sketch, "E95.MirrorC", {"center": v(0, -120) * mm, "radius": 6 * mm});
            skSolve(sketch);
        }
        {
            var Q0;
            {var subQ4=sQuery(id+"F16.wireOp",EDGE,"E86");Q0=makeQuery(id+"F16.imprint","IMPRINT",FACE,{"disambiguationData":[TD([[makeQuery(id+"F16.imprint","IMPRINT",EDGE,{"derivedFrom":subQ4}),-1.0]])]});}
            var Q1;
            Q1=makeQuery(id+"F16.imprint","IMPRINT",FACE,{"disambiguationData":[TD([[makeQuery(id+"F16.imprint","IMPRINT",EDGE,{"derivedFrom":sQuery(id+"F16.wireOp",EDGE,"E88.MirrorCS")}),-1.0]])]});
            var Q2;
            Q2=makeQuery(id+"F16.imprint","IMPRINT",FACE,{"disambiguationData":[TD([[makeQuery(id+"F16.imprint","IMPRINT",EDGE,{"derivedFrom":sQuery(id+"F16.wireOp",EDGE,"E80")}),-1.0]])]});
            var Q3;
            Q3=makeQuery(id+"F2.opExtrude","CAP_FACE",FACE,{"disambiguationData":[OSD([sQuery(id+"F0.wireOp",EDGE,"E12"),sQuery(id+"F0.wireOp",EDGE,"E13"),sQuery(id+"F0.wireOp",EDGE,"E14"),sQuery(id+"F0.wireOp",EDGE,"E15"),sQuery(id+"F0.wireOp",EDGE,"E17.filletArc"),sQuery(id+"F0.wireOp",EDGE,"E18.filletArc"),sQuery(id+"F0.wireOp",EDGE,"E19.filletArc"),sQuery(id+"F0.wireOp",EDGE,"E20.filletArc"),sQuery(id+"F0.wireOp",EDGE,"E25.0"),sQuery(id+"F0.wireOp",EDGE,"E25.1"),sQuery(id+"F0.wireOp",EDGE,"E25.2"),sQuery(id+"F0.wireOp",EDGE,"E25.3"),sQuery(id+"F0.wireOp",EDGE,"E25.4"),sQuery(id+"F0.wireOp",EDGE,"E25.5"),sQuery(id+"F0.wireOp",EDGE,"E25.6"),sQuery(id+"F0.wireOp",EDGE,"E25.7")])],"isStart":false});
            extrude(context, id + "F17", {"entities" : qUnion([Q0, Q1, Q2]), "endBound" : BoundingType.UP_TO_SURFACE, "depth" : 25 * mm, "endBoundEntityFace" : qUnion([Q3]), "offsetDistance" : 25 * mm});
        }
    });
